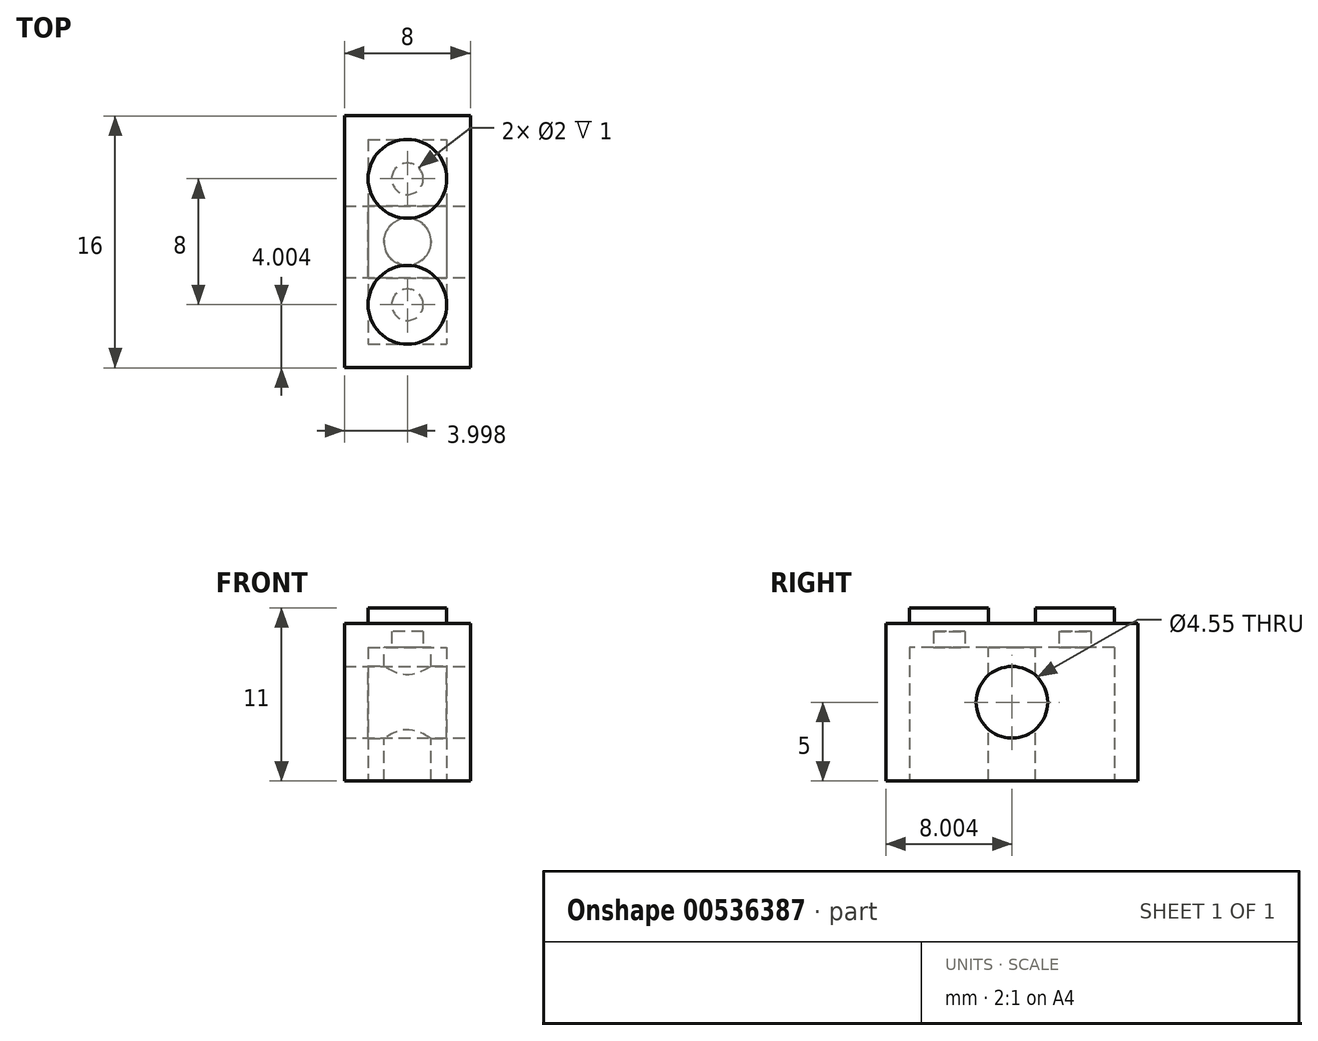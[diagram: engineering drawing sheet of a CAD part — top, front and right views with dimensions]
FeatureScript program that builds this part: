
annotation { "Feature Type Name" : "Feature", "Feature Type Description" : "" }
export const myFeature = defineFeature(function(context is Context, id is Id, definition is map)
    precondition{}
    {
        {
            var Q0;
            Q0=qCreatedBy(makeId("Top.planeOp"),FACE);
            var sketch = newSketch(context, id + "F0", { "sketchPlane" : qUnion([Q0])});
            skLineSegment(sketch, "E0.bottom", {"start": v(-10.52, 19.44) * mm, "end": v(-2.52, 19.44) * mm});
            skLineSegment(sketch, "E0.top", {"start": v(-10.52, 3.44) * mm, "end": v(-2.52, 3.44) * mm});
            skLineSegment(sketch, "E0.left", {"start": v(-10.52, 19.44) * mm, "end": v(-10.52, 3.44) * mm});
            skLineSegment(sketch, "E0.right", {"start": v(-2.52, 19.44) * mm, "end": v(-2.52, 3.44) * mm});
            skSolve(sketch);
        }
        {
            var Q0;
            Q0=makeQuery(id+"F0.imprint","IMPRINT",FACE,{"disambiguationData":[TD([[makeQuery(id+"F0.imprint","IMPRINT",EDGE,{"derivedFrom":sQuery(id+"F0.wireOp",EDGE,"E0.bottom")}),-1.0]])]});
            extrude(context, id + "F1", {"entities" : qUnion([Q0]), "depth" : 10 * mm, "offsetDistance" : 25 * mm});
        }
        {
            var Q0;
            Q0=makeQuery(id+"F1.opExtrude","CAP_FACE",FACE,{"disambiguationData":[OSD([sQuery(id+"F0.wireOp",EDGE,"E0.bottom"),sQuery(id+"F0.wireOp",EDGE,"E0.top"),sQuery(id+"F0.wireOp",EDGE,"E0.left"),sQuery(id+"F0.wireOp",EDGE,"E0.right")])],"isStart":false});
            var sketch = newSketch(context, id + "F2", { "sketchPlane" : qUnion([Q0])});
            skCircle(sketch, "E1", {"center": v(-6.52, 7.44) * mm, "radius": 2.5 * mm});
            skPoint(sketch, "E1.centerSnap0", {"position": v(-6.52, 3.44) * mm});
            skCircle(sketch, "E2", {"center": v(-6.52, 15.44) * mm, "radius": 2.5 * mm});
            skPoint(sketch, "E2.centerSnap0", {"position": v(-6.52, 19.44) * mm});
            skSolve(sketch);
        }
        {
            var Q0;
            Q0=makeQuery(id+"F2.imprint","IMPRINT",FACE,{"disambiguationData":[TD([[makeQuery(id+"F2.imprint","IMPRINT",EDGE,{"derivedFrom":sQuery(id+"F2.wireOp",EDGE,"E1")}),1.0]])]});
            var Q1;
            Q1=makeQuery(id+"F2.imprint","IMPRINT",FACE,{"disambiguationData":[TD([[makeQuery(id+"F2.imprint","IMPRINT",EDGE,{"derivedFrom":sQuery(id+"F2.wireOp",EDGE,"E2")}),1.0]])]});
            extrude(context, id + "F3", {"entities" : qUnion([Q0, Q1]), "operationType" : NewBodyOperationType.ADD, "depth" : 1 * mm, "offsetDistance" : 25 * mm});
        }
        {
            var Q0;
            Q0=makeQuery(id+"F1.opExtrude","CAP_FACE",FACE,{"disambiguationData":[OSD([sQuery(id+"F0.wireOp",EDGE,"E0.bottom"),sQuery(id+"F0.wireOp",EDGE,"E0.top"),sQuery(id+"F0.wireOp",EDGE,"E0.left"),sQuery(id+"F0.wireOp",EDGE,"E0.right")])],"isStart":true});
            shell(context, id + "F4", {"entities" : qUnion([Q0]), "thickness" : 1.5 * mm});
        }
        {
            var Q0;
            Q0=makeQuery(id+"F1.opExtrude","CAP_FACE",FACE,{"disambiguationData":[OSD([sQuery(id+"F0.wireOp",EDGE,"E0.bottom"),sQuery(id+"F0.wireOp",EDGE,"E0.top"),sQuery(id+"F0.wireOp",EDGE,"E0.left"),sQuery(id+"F0.wireOp",EDGE,"E0.right")])],"isStart":false});
            var sketch = newSketch(context, id + "F5", { "sketchPlane" : qUnion([Q0])});
            skCircle(sketch, "E3", {"center": v(-6.52, 11.44) * mm, "radius": 1.5 * mm});
            skPoint(sketch, "E3.centerSnap0", {"position": v(-6.52, 3.44) * mm});
            skPoint(sketch, "E3.centerSnap1", {"position": v(-10.52, 11.44) * mm});
            skSolve(sketch);
        }
        {
            var Q0;
            {var subQ0=sQuery(id+"F5.wireOp",EDGE,"E3");var subQ1=makeQuery(id+"F5.imprint","INTERSECT",VERTEX,{"derivedFrom":[makeQuery(id+"F3.opExtrude","CAP_EDGE",EDGE,{"disambiguationData":[OSD([sQuery(id+"F2.wireOp",EDGE,"E1")])],"isStart":true}),subQ0]});Q0=makeQuery(id+"F5.imprint","IMPRINT",FACE,{"disambiguationData":[TD([[makeQuery(id+"F5.imprint","IMPRINT",EDGE,{"disambiguationData":[TD([[subQ1,1.0]])],"derivedFrom":subQ0}),1.0]])]});}
            var Q1;
            Q1=sQuery(id+"F5.wireOp",EDGE,"E3");
            extrude(context, id + "F6", {"entities" : qUnion([Q0]), "operationType" : NewBodyOperationType.ADD, "surfaceEntities" : qUnion([Q1]), "oppositeDirection" : true, "depth" : 10 * mm, "offsetDistance" : 25 * mm});
        }
        {
            var Q0;
            Q0=makeQuery(id+"F1.opExtrude","SWEPT_FACE",FACE,{"disambiguationData":[OSD([sQuery(id+"F0.wireOp",EDGE,"E0.right")])]});
            var sketch = newSketch(context, id + "F7", { "sketchPlane" : qUnion([Q0])});
            skCircle(sketch, "E4", {"center": v(11.44, 5) * mm, "radius": 2.3 * mm});
            skPoint(sketch, "E4.centerSnap0", {"position": v(11.44, 0) * mm});
            skPoint(sketch, "E4.centerSnap1", {"position": v(3.44, 5) * mm});
            skCircle(sketch, "E5", {"center": v(11.44, 5) * mm, "radius": 2.27 * mm});
            skSolve(sketch);
        }
        {
            var Q0;
            Q0=makeQuery(id+"F7.imprint","IMPRINT",FACE,{"disambiguationData":[TD([[makeQuery(id+"F7.imprint","IMPRINT",EDGE,{"derivedFrom":sQuery(id+"F7.wireOp",EDGE,"E4")}),1.0]])]});
            extrude(context, id + "F8", {"entities" : qUnion([Q0]), "operationType" : NewBodyOperationType.ADD, "oppositeDirection" : true, "depth" : 8 * mm, "offsetDistance" : 25 * mm});
        }
        {
            var Q0;
            Q0=makeQuery(id+"F7.imprint","IMPRINT",FACE,{"disambiguationData":[TD([[makeQuery(id+"F7.imprint","IMPRINT",EDGE,{"derivedFrom":sQuery(id+"F7.wireOp",EDGE,"E5")}),1.0]])]});
            extrude(context, id + "F9", {"entities" : qUnion([Q0]), "operationType" : NewBodyOperationType.REMOVE, "oppositeDirection" : true, "depth" : 8 * mm, "offsetDistance" : 25 * mm});
        }
    });
